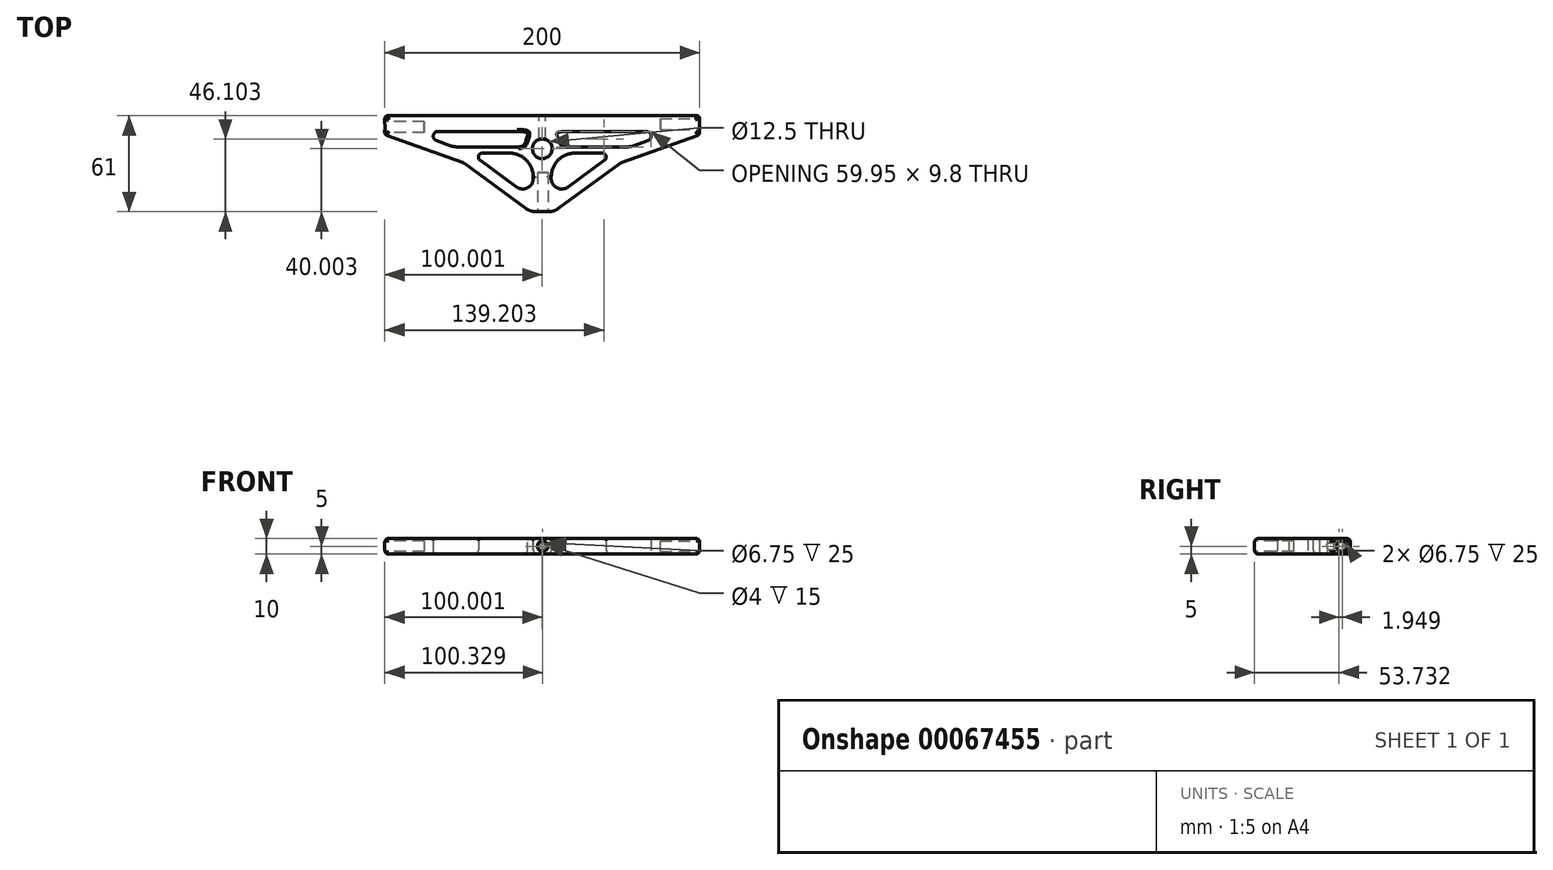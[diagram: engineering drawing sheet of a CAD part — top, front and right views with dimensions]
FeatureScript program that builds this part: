
annotation { "Feature Type Name" : "Feature", "Feature Type Description" : "" }
export const myFeature = defineFeature(function(context is Context, id is Id, definition is map)
    precondition{}
    {
        {
            var Q0;
            Q0=qCreatedBy(makeId("Top.planeOp"),FACE);
            var sketch = newSketch(context, id + "F0", { "sketchPlane" : qUnion([Q0])});
            skLineSegment(sketch, "E0", {"start": v(-164.89, -38.66) * mm, "end": v(35.11, -38.66) * mm, "construction": true});
            skCircle(sketch, "E1", {"center": v(-64.89, -53.66) * mm, "radius": 6.25 * mm});
            skPoint(sketch, "E2", {"position": v(-64.89, -38.66) * mm});
            skLineSegment(sketch, "E3", {"start": v(-164.89, -43.25) * mm, "end": v(-164.89, -34.66) * mm});
            skLineSegment(sketch, "E4", {"start": v(-162.89, -32.66) * mm, "end": v(33.11, -32.66) * mm});
            skLineSegment(sketch, "E5", {"start": v(35.11, -34.66) * mm, "end": v(35.11, -43.25) * mm});
            skLineSegment(sketch, "E6", {"start": v(33.79, -45.13) * mm, "end": v(-14.62, -62.56) * mm});
            skLineSegment(sketch, "E7", {"start": v(-15.12, -62.83) * mm, "end": v(-54.76, -91.74) * mm});
            skLineSegment(sketch, "E8", {"start": v(-75.02, -91.74) * mm, "end": v(-114.66, -62.83) * mm});
            skLineSegment(sketch, "E9", {"start": v(-115.16, -62.56) * mm, "end": v(-163.57, -45.13) * mm});
            skPoint(sketch, "E10.visualSharp", {"position": v(-164.89, -32.66) * mm});
            skArc(sketch, "E10.filletArc", {"start": v(-162.89, -32.66) * mm, "mid": v(-164.3, -33.24) * mm, "end": v(-164.89, -34.66) * mm});
            skPoint(sketch, "E11.visualSharp", {"position": v(-114.89, -62.66) * mm});
            skArc(sketch, "E11.filletArc", {"start": v(-114.66, -62.83) * mm, "mid": v(-114.9, -62.67) * mm, "end": v(-115.16, -62.56) * mm});
            skPoint(sketch, "E12.visualSharp", {"position": v(-14.89, -62.66) * mm});
            skArc(sketch, "E12.filletArc", {"start": v(-14.62, -62.56) * mm, "mid": v(-14.88, -62.67) * mm, "end": v(-15.12, -62.83) * mm});
            skPoint(sketch, "E13.visualSharp", {"position": v(35.11, -44.66) * mm});
            skArc(sketch, "E13.filletArc", {"start": v(33.79, -45.13) * mm, "mid": v(34.75, -44.4) * mm, "end": v(35.11, -43.25) * mm});
            skPoint(sketch, "E14.visualSharp", {"position": v(-164.89, -44.66) * mm});
            skArc(sketch, "E14.filletArc", {"start": v(-164.89, -43.25) * mm, "mid": v(-164.53, -44.4) * mm, "end": v(-163.57, -45.13) * mm});
            skPoint(sketch, "E15.visualSharp", {"position": v(35.11, -32.66) * mm});
            skArc(sketch, "E15.filletArc", {"start": v(35.11, -34.66) * mm, "mid": v(34.52, -33.24) * mm, "end": v(33.11, -32.66) * mm});
            skLineSegment(sketch, "E16", {"start": v(-69.13, -93.66) * mm, "end": v(-60.65, -93.66) * mm});
            skPoint(sketch, "E17", {"position": v(-64.89, -93.66) * mm});
            skPoint(sketch, "E18.visualSharp", {"position": v(-72.39, -93.66) * mm});
            skArc(sketch, "E18.filletArc", {"start": v(-75.02, -91.74) * mm, "mid": v(-72.23, -93.16) * mm, "end": v(-69.13, -93.66) * mm});
            skPoint(sketch, "E19.visualSharp", {"position": v(-57.39, -93.66) * mm});
            skArc(sketch, "E19.filletArc", {"start": v(-60.65, -93.66) * mm, "mid": v(-57.55, -93.16) * mm, "end": v(-54.76, -91.74) * mm});
            skLineSegment(sketch, "E20", {"start": v(-132.13, -48.48) * mm, "end": v(-122.72, -51.87) * mm});
            skLineSegment(sketch, "E21", {"start": v(-119.33, -52.46) * mm, "end": v(-79.8, -52.46) * mm});
            skLineSegment(sketch, "E22", {"start": v(-80.77, -42.66) * mm, "end": v(-131.11, -42.66) * mm});
            skLineSegment(sketch, "E23", {"start": v(-81.22, -77.93) * mm, "end": v(-104.45, -61) * mm});
            skLineSegment(sketch, "E24", {"start": v(-102.97, -56.46) * mm, "end": v(-85.62, -56.46) * mm});
            skPoint(sketch, "E25.visualSharp", {"position": v(-121.08, -52.46) * mm});
            skArc(sketch, "E25.filletArc", {"start": v(-122.72, -51.87) * mm, "mid": v(-121.05, -52.3) * mm, "end": v(-119.33, -52.46) * mm});
            skPoint(sketch, "E26.visualSharp", {"position": v(-148.3, -42.66) * mm});
            skArc(sketch, "E26.filletArc", {"start": v(-131.11, -42.66) * mm, "mid": v(-134.07, -45.14) * mm, "end": v(-132.13, -48.48) * mm});
            skPoint(sketch, "E27.visualSharp", {"position": v(-71.68, -52.46) * mm});
            skPoint(sketch, "E28.visualSharp", {"position": v(-70.62, -56.46) * mm});
            skArc(sketch, "E28.filletArc", {"start": v(-70.62, -71.71) * mm, "mid": v(-74.92, -60.94) * mm, "end": v(-85.62, -56.46) * mm});
            skPoint(sketch, "E29.visualSharp", {"position": v(-110.66, -56.46) * mm});
            skArc(sketch, "E29.filletArc", {"start": v(-102.97, -56.46) * mm, "mid": v(-105.35, -58.19) * mm, "end": v(-104.45, -61) * mm});
            skPoint(sketch, "E30.visualSharp", {"position": v(-69.37, -86.58) * mm});
            skArc(sketch, "E30.filletArc", {"start": v(-81.22, -77.93) * mm, "mid": v(-73.88, -78.3) * mm, "end": v(-70.62, -71.71) * mm});
            skLineSegment(sketch, "E31", {"start": v(-64.89, -15.97) * mm, "end": v(-64.89, -129.5) * mm, "construction": true});
            skLineSegment(sketch, "E32.MirrorCS", {"start": v(-52.74, -48.63) * mm, "end": v(-52.74, -48.63) * mm});
            skLineSegment(sketch, "E33.MirrorCS", {"start": v(-26.81, -56.46) * mm, "end": v(-44.16, -56.46) * mm});
            skLineSegment(sketch, "E34.MirrorCS", {"start": v(-48.56, -77.93) * mm, "end": v(-25.33, -61) * mm});
            skArc(sketch, "E35.MirrorCS", {"start": v(-59.16, -71.71) * mm, "mid": v(-54.86, -60.94) * mm, "end": v(-44.16, -56.46) * mm});
            skArc(sketch, "E36.MirrorCS", {"start": v(-48.56, -77.93) * mm, "mid": v(-55.9, -78.3) * mm, "end": v(-59.16, -71.71) * mm});
            skArc(sketch, "E37.MirrorCS", {"start": v(-26.81, -56.46) * mm, "mid": v(-24.43, -58.19) * mm, "end": v(-25.33, -61) * mm});
            skFitSpline(sketch, "E38", {"points": [v(-80.77, -42.66) * mm, v(-74.53, -46.12) * mm, v(-79.8, -52.46) * mm], "startDerivative": vector(49.6, 0) * mm, "endDerivative": vector(-24.17, 0) * mm});
            skFitSpline(sketch, "E39.MirrorCS", {"points": [v(-49.01, -42.66) * mm, v(-55.25, -46.12) * mm, v(-49.97, -52.46) * mm], "startDerivative": vector(-49.6, 0) * mm, "endDerivative": vector(24.17, 0) * mm});
            skLineSegment(sketch, "E40.MirrorCS", {"start": v(-10.45, -52.46) * mm, "end": v(-49.97, -52.46) * mm});
            skArc(sketch, "E41.MirrorCS", {"start": v(-7.06, -51.87) * mm, "mid": v(-8.73, -52.3) * mm, "end": v(-10.45, -52.46) * mm});
            skLineSegment(sketch, "E42.MirrorCS", {"start": v(-49.01, -42.66) * mm, "end": v(1.33, -42.66) * mm});
            skLineSegment(sketch, "E43.MirrorCS", {"start": v(2.35, -48.48) * mm, "end": v(-7.06, -51.87) * mm});
            skArc(sketch, "E44.MirrorCS", {"start": v(1.33, -42.66) * mm, "mid": v(4.29, -45.14) * mm, "end": v(2.35, -48.48) * mm});
            skSolve(sketch);
        }
        {
            var Q0;
            Q0=makeQuery(id+"F0.imprint","IMPRINT",FACE,{"disambiguationData":[TD([[makeQuery(id+"F0.imprint","IMPRINT",EDGE,{"derivedFrom":sQuery(id+"F0.wireOp",EDGE,"E1")}),-1.0]])]});
            extrude(context, id + "F1", {"entities" : qUnion([Q0]), "depth" : 10 * mm});
        }
        {
            var Q0;
            Q0=makeQuery(id+"F1.opExtrude","SWEPT_FACE",FACE,{"disambiguationData":[OSD([sQuery(id+"F0.wireOp",EDGE,"E5")])]});
            var sketch = newSketch(context, id + "F2", { "sketchPlane" : qUnion([Q0])});
            skCircle(sketch, "E45", {"center": v(-37.98, 5) * mm, "radius": 3.38 * mm});
            skPoint(sketch, "E45.centerSnap0", {"position": v(-37.98, 2) * mm});
            skPoint(sketch, "E45.centerSnap1", {"position": v(-34.66, 5) * mm});
            skSolve(sketch);
        }
        {
            var Q0;
            Q0 = qSketchRegion(id + "F2", true);
            extrude(context, id + "F3", {"entities" : qUnion([Q0]), "operationType" : NewBodyOperationType.REMOVE, "oppositeDirection" : true, "depth" : 25 * mm});
        }
        {
            var Q0;
            Q0=makeQuery(id+"F1.opExtrude","SWEPT_FACE",FACE,{"disambiguationData":[OSD([sQuery(id+"F0.wireOp",EDGE,"E3")])]});
            var sketch = newSketch(context, id + "F4", { "sketchPlane" : qUnion([Q0])});
            skCircle(sketch, "E46", {"center": v(39.93, 5) * mm, "radius": 3.38 * mm});
            skPoint(sketch, "E46.centerSnap0", {"position": v(43.25, 5) * mm});
            skPoint(sketch, "E46.centerSnap1", {"position": v(39.93, 8) * mm});
            skSolve(sketch);
        }
        {
            var Q0;
            Q0 = qSketchRegion(id + "F4", true);
            extrude(context, id + "F5", {"entities" : qUnion([Q0]), "operationType" : NewBodyOperationType.REMOVE, "oppositeDirection" : true, "depth" : 25 * mm});
        }
        {
            var Q0;
            Q0=makeQuery(id+"F1.opExtrude","SWEPT_FACE",FACE,{"disambiguationData":[OSD([sQuery(id+"F0.wireOp",EDGE,"E16")])]});
            var sketch = newSketch(context, id + "F6", { "sketchPlane" : qUnion([Q0])});
            skCircle(sketch, "E47", {"center": v(-64.56, 5) * mm, "radius": 3.38 * mm});
            skPoint(sketch, "E47.centerSnap0", {"position": v(-60.65, 5) * mm});
            skPoint(sketch, "E47.centerSnap1", {"position": v(-64.56, 8) * mm});
            skSolve(sketch);
        }
        {
            var Q0;
            Q0 = qSketchRegion(id + "F6", true);
            extrude(context, id + "F7", {"entities" : qUnion([Q0]), "operationType" : NewBodyOperationType.REMOVE, "oppositeDirection" : true, "depth" : 25 * mm});
        }
        {
            var Q0;
            Q0=makeQuery(id+"F1.opExtrude","SWEPT_FACE",FACE,{"disambiguationData":[OSD([sQuery(id+"F0.wireOp",EDGE,"E4")])]});
            var sketch = newSketch(context, id + "F8", { "sketchPlane" : qUnion([Q0])});
            skCircle(sketch, "E48", {"center": v(64.89, 5) * mm, "radius": 2 * mm});
            skPoint(sketch, "E48.centerSnap0", {"position": v(64.89, 8) * mm});
            skPoint(sketch, "E48.centerSnap1", {"position": v(-33.11, 5) * mm});
            skSolve(sketch);
        }
        {
            var Q0;
            Q0 = qSketchRegion(id + "F8", true);
            extrude(context, id + "F9", {"entities" : qUnion([Q0]), "operationType" : NewBodyOperationType.REMOVE, "oppositeDirection" : true, "depth" : 15 * mm});
        }
        {
            var Q0;
            Q0=makeQuery(id+"F1.opExtrude","CAP_EDGE",EDGE,{"disambiguationData":[OSD([sQuery(id+"F0.wireOp",EDGE,"E21")])],"isStart":false});
            var Q1;
            Q1=makeQuery(id+"F1.opExtrude","CAP_EDGE",EDGE,{"disambiguationData":[OSD([sQuery(id+"F0.wireOp",EDGE,"E25.filletArc")])],"isStart":false});
            var Q2;
            Q2=makeQuery(id+"F1.opExtrude","CAP_EDGE",EDGE,{"disambiguationData":[OSD([sQuery(id+"F0.wireOp",EDGE,"E20")])],"isStart":false});
            var Q3;
            Q3=makeQuery(id+"F1.opExtrude","CAP_EDGE",EDGE,{"disambiguationData":[OSD([sQuery(id+"F0.wireOp",EDGE,"E26.filletArc")])],"isStart":false});
            var Q4;
            Q4=makeQuery(id+"F1.opExtrude","CAP_EDGE",EDGE,{"disambiguationData":[OSD([sQuery(id+"F0.wireOp",EDGE,"E22")])],"isStart":false});
            var Q5;
            Q5=makeQuery(id+"F1.opExtrude","CAP_EDGE",EDGE,{"disambiguationData":[OSD([sQuery(id+"F0.wireOp",EDGE,"64b9a609-9918-46ae-89ac-6a62835a1d1d.filletArc")])],"isStart":false});
            var Q6;
            Q6=makeQuery(id+"F1.opExtrude","CAP_EDGE",EDGE,{"disambiguationData":[OSD([sQuery(id+"F0.wireOp",EDGE,"E27.filletArc")])],"isStart":false});
            var Q7;
            Q7=makeQuery(id+"F1.opExtrude","CAP_EDGE",EDGE,{"disambiguationData":[OSD([sQuery(id+"F0.wireOp",EDGE,"9bb5a563-58ea-4804-b1da-0b5fba09ffe80.MirrorCS")])],"isStart":false});
            var Q8;
            Q8=makeQuery(id+"F1.opExtrude","CAP_EDGE",EDGE,{"disambiguationData":[OSD([sQuery(id+"F0.wireOp",EDGE,"26685e91-07d7-4c1d-ad4d-5f948c7a271e0.MirrorCS")])],"isStart":false});
            var Q9;
            Q9=makeQuery(id+"F1.opExtrude","CAP_EDGE",EDGE,{"disambiguationData":[OSD([sQuery(id+"F0.wireOp",EDGE,"E32.MirrorCS")])],"isStart":false});
            var Q10;
            Q10=makeQuery(id+"F1.opExtrude","CAP_EDGE",EDGE,{"disambiguationData":[OSD([sQuery(id+"F0.wireOp",EDGE,"23dGFq8F-n6bw-VskO-3L1m-OVhaivIuo1WI")])],"isStart":false});
            var Q11;
            Q11=makeQuery(id+"F1.opExtrude","CAP_EDGE",EDGE,{"disambiguationData":[OSD([sQuery(id+"F0.wireOp",EDGE,"5624469e-30fd-4980-9fb2-801fae8b7fbf0.MirrorCS")])],"isStart":false});
            var Q12;
            Q12=makeQuery(id+"F1.opExtrude","CAP_EDGE",EDGE,{"disambiguationData":[OSD([sQuery(id+"F0.wireOp",EDGE,"e43e02d5-dfc4-401d-9f2f-5ade6926303f0.MirrorCS")])],"isStart":false});
            var Q13;
            Q13=makeQuery(id+"F1.opExtrude","CAP_EDGE",EDGE,{"disambiguationData":[OSD([sQuery(id+"F0.wireOp",EDGE,"ed1df8a4-d5b6-4147-8766-64a3af826c070.MirrorCS")])],"isStart":false});
            var Q14;
            Q14=makeQuery(id+"F1.opExtrude","CAP_EDGE",EDGE,{"disambiguationData":[OSD([sQuery(id+"F0.wireOp",EDGE,"1d803a3b-767e-4f32-a2c7-10c3e793d6170.MirrorCS")])],"isStart":false});
            var Q15;
            Q15=makeQuery(id+"F1.opExtrude","CAP_EDGE",EDGE,{"disambiguationData":[OSD([sQuery(id+"F0.wireOp",EDGE,"aa5615ff-1bb6-4136-8914-040205da53280.MirrorCS")])],"isStart":false});
            var Q16;
            Q16=makeQuery(id+"F1.opExtrude","CAP_EDGE",EDGE,{"disambiguationData":[OSD([sQuery(id+"F0.wireOp",EDGE,"E33.MirrorCS")])],"isStart":false});
            var Q17;
            Q17=makeQuery(id+"F1.opExtrude","CAP_EDGE",EDGE,{"disambiguationData":[OSD([sQuery(id+"F0.wireOp",EDGE,"E37.MirrorCS")])],"isStart":false});
            var Q18;
            Q18=makeQuery(id+"F1.opExtrude","CAP_EDGE",EDGE,{"disambiguationData":[OSD([sQuery(id+"F0.wireOp",EDGE,"E34.MirrorCS")])],"isStart":false});
            var Q19;
            Q19=makeQuery(id+"F1.opExtrude","CAP_EDGE",EDGE,{"disambiguationData":[OSD([sQuery(id+"F0.wireOp",EDGE,"E36.MirrorCS")])],"isStart":false});
            var Q20;
            Q20=makeQuery(id+"F1.opExtrude","CAP_EDGE",EDGE,{"disambiguationData":[OSD([sQuery(id+"F0.wireOp",EDGE,"95280304-b442-4904-95d4-ad25dd71f5a00.MirrorCS")])],"isStart":false});
            var Q21;
            Q21=makeQuery(id+"F1.opExtrude","CAP_EDGE",EDGE,{"disambiguationData":[OSD([sQuery(id+"F0.wireOp",EDGE,"E35.MirrorCS")])],"isStart":false});
            var Q22;
            Q22=makeQuery(id+"F1.opExtrude","CAP_EDGE",EDGE,{"disambiguationData":[OSD([sQuery(id+"F0.wireOp",EDGE,"E28.filletArc")])],"isStart":false});
            var Q23;
            Q23=makeQuery(id+"F1.opExtrude","CAP_EDGE",EDGE,{"disambiguationData":[OSD([sQuery(id+"F0.wireOp",EDGE,"43XHimmo-ow6s-nS2Q-KjjI-esJLu0zPwdxe")])],"isStart":false});
            var Q24;
            Q24=makeQuery(id+"F1.opExtrude","CAP_EDGE",EDGE,{"disambiguationData":[OSD([sQuery(id+"F0.wireOp",EDGE,"E30.filletArc")])],"isStart":false});
            var Q25;
            Q25=makeQuery(id+"F1.opExtrude","CAP_EDGE",EDGE,{"disambiguationData":[OSD([sQuery(id+"F0.wireOp",EDGE,"E23")])],"isStart":false});
            var Q26;
            Q26=makeQuery(id+"F1.opExtrude","CAP_EDGE",EDGE,{"disambiguationData":[OSD([sQuery(id+"F0.wireOp",EDGE,"E29.filletArc")])],"isStart":false});
            var Q27;
            Q27=makeQuery(id+"F1.opExtrude","CAP_EDGE",EDGE,{"disambiguationData":[OSD([sQuery(id+"F0.wireOp",EDGE,"E24")])],"isStart":false});
            fillet(context, id + "F10", {"entities" : qUnion([Q0, Q1, Q2, Q3, Q4, Q5, Q6, Q7, Q8, Q9, Q10, Q11, Q12, Q13, Q14, Q15, Q16, Q17, Q18, Q19, Q20, Q21, Q22, Q23, Q24, Q25, Q26, Q27]), "radius" : 1.2 * mm, "tangentPropagation" : true, "allowEdgeOverflow" : false});
        }
        {
            var Q0;
            Q0=makeQuery(id+"F1.opExtrude","CAP_EDGE",EDGE,{"disambiguationData":[OSD([sQuery(id+"F0.wireOp",EDGE,"E4")])],"isStart":false});
            var Q1;
            Q1=makeQuery(id+"F1.opExtrude","CAP_EDGE",EDGE,{"disambiguationData":[OSD([sQuery(id+"F0.wireOp",EDGE,"E4")])],"isStart":true});
            fillet(context, id + "F11", {"entities" : qUnion([Q0, Q1]), "radius" : 2.5 * mm, "tangentPropagation" : true, "allowEdgeOverflow" : false});
        }
        {
            var Q0;
            Q0=makeQuery(id+"F1.opExtrude","CAP_EDGE",EDGE,{"disambiguationData":[OSD([sQuery(id+"F0.wireOp",EDGE,"5624469e-30fd-4980-9fb2-801fae8b7fbf0.MirrorCS")])],"isStart":true});
            var Q1;
            Q1=makeQuery(id+"F1.opExtrude","CAP_EDGE",EDGE,{"disambiguationData":[OSD([sQuery(id+"F0.wireOp",EDGE,"E35.MirrorCS")])],"isStart":true});
            var Q2;
            Q2=makeQuery(id+"F1.opExtrude","CAP_EDGE",EDGE,{"disambiguationData":[OSD([sQuery(id+"F0.wireOp",EDGE,"E28.filletArc")])],"isStart":true});
            var Q3;
            Q3=makeQuery(id+"F1.opExtrude","CAP_EDGE",EDGE,{"disambiguationData":[OSD([sQuery(id+"F0.wireOp",EDGE,"E27.filletArc")])],"isStart":true});
            fillet(context, id + "F12", {"entities" : qUnion([Q0, Q1, Q2, Q3]), "radius" : 3 * mm, "tangentPropagation" : true, "allowEdgeOverflow" : false});
        }
    });
